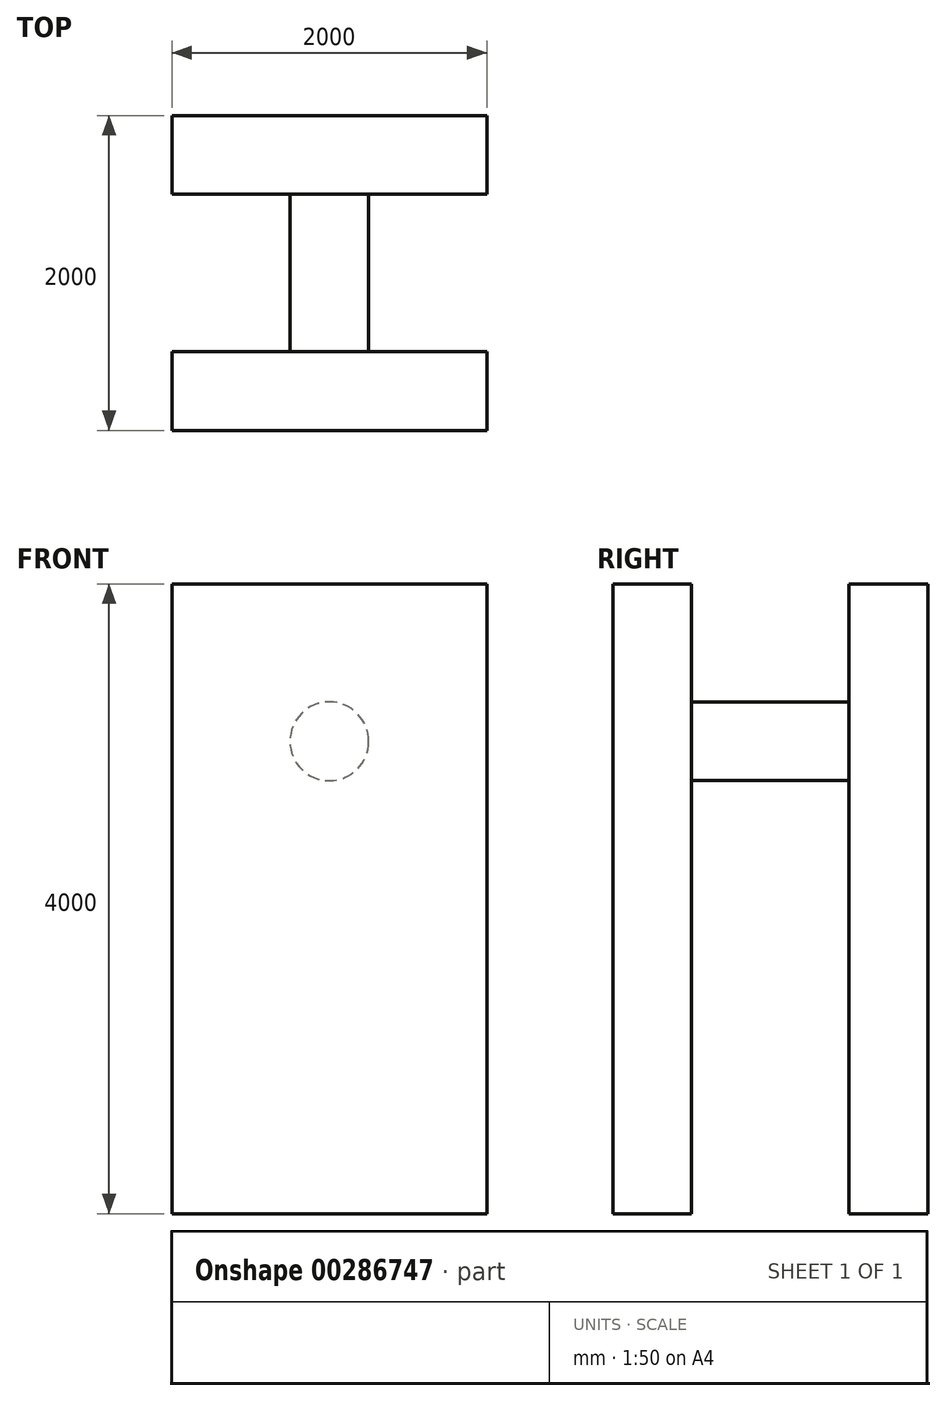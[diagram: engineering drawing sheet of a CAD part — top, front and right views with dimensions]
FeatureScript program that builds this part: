
annotation { "Feature Type Name" : "Feature", "Feature Type Description" : "" }
export const myFeature = defineFeature(function(context is Context, id is Id, definition is map)
    precondition{}
    {
        {
            var Q0;
            Q0=qCreatedBy(makeId("Front.planeOp"),FACE);
            var sketch = newSketch(context, id + "F0", { "sketchPlane" : qUnion([Q0])});
            skLineSegment(sketch, "E0.bottom", {"start": v(0, 0) * mm, "end": v(2000, 0) * mm});
            skLineSegment(sketch, "E0.top", {"start": v(0, 4000) * mm, "end": v(2000, 4000) * mm});
            skLineSegment(sketch, "E0.left", {"start": v(0, 0) * mm, "end": v(0, 4000) * mm});
            skLineSegment(sketch, "E0.right", {"start": v(2000, 0) * mm, "end": v(2000, 4000) * mm});
            skSolve(sketch);
        }
        {
            var Q0;
            Q0=makeQuery(id+"F0.imprint","IMPRINT",FACE,{"disambiguationData":[TD([[makeQuery(id+"F0.imprint","IMPRINT",EDGE,{"derivedFrom":sQuery(id+"F0.wireOp",EDGE,"E0.bottom")}),1.0]])]});
            extrude(context, id + "F1", {"entities" : qUnion([Q0]), "depth" : 500 * mm});
        }
        {
            var Q0;
            Q0=makeQuery(id+"F1.opExtrude","CAP_FACE",FACE,{"disambiguationData":[OSD([sQuery(id+"F0.wireOp",EDGE,"E0.bottom"),sQuery(id+"F0.wireOp",EDGE,"E0.top"),sQuery(id+"F0.wireOp",EDGE,"E0.left"),sQuery(id+"F0.wireOp",EDGE,"E0.right")])],"isStart":false});
            var sketch = newSketch(context, id + "F2", { "sketchPlane" : qUnion([Q0])});
            skCircle(sketch, "E1", {"center": v(1000, 3000) * mm, "radius": 250 * mm});
            skSolve(sketch);
        }
        {
            var Q0;
            Q0=makeQuery(id+"F2.imprint","IMPRINT",FACE,{"disambiguationData":[TD([[makeQuery(id+"F2.imprint","IMPRINT",EDGE,{"derivedFrom":sQuery(id+"F2.wireOp",EDGE,"E1")}),1.0]])]});
            extrude(context, id + "F3", {"entities" : qUnion([Q0]), "operationType" : NewBodyOperationType.ADD, "depth" : 1000 * mm});
        }
        {
            var Q0;
            Q0=makeQuery(id+"F3.opExtrude","CAP_FACE",FACE,{"disambiguationData":[OSD([sQuery(id+"F2.wireOp",EDGE,"E1")])],"isStart":false});
            var sketch = newSketch(context, id + "F4", { "sketchPlane" : qUnion([Q0])});
            skLineSegment(sketch, "E2.bottom", {"start": v(0, 0) * mm, "end": v(2000, 0) * mm});
            skLineSegment(sketch, "E2.top", {"start": v(0, 4000) * mm, "end": v(2000, 4000) * mm});
            skLineSegment(sketch, "E2.left", {"start": v(0, 0) * mm, "end": v(0, 4000) * mm});
            skLineSegment(sketch, "E2.right", {"start": v(2000, 0) * mm, "end": v(2000, 4000) * mm});
            skSolve(sketch);
        }
        {
            var Q0;
            Q0 = qSketchRegion(id + "F4", true);
            extrude(context, id + "F5", {"entities" : qUnion([Q0]), "operationType" : NewBodyOperationType.ADD, "depth" : 500 * mm});
        }
    });
